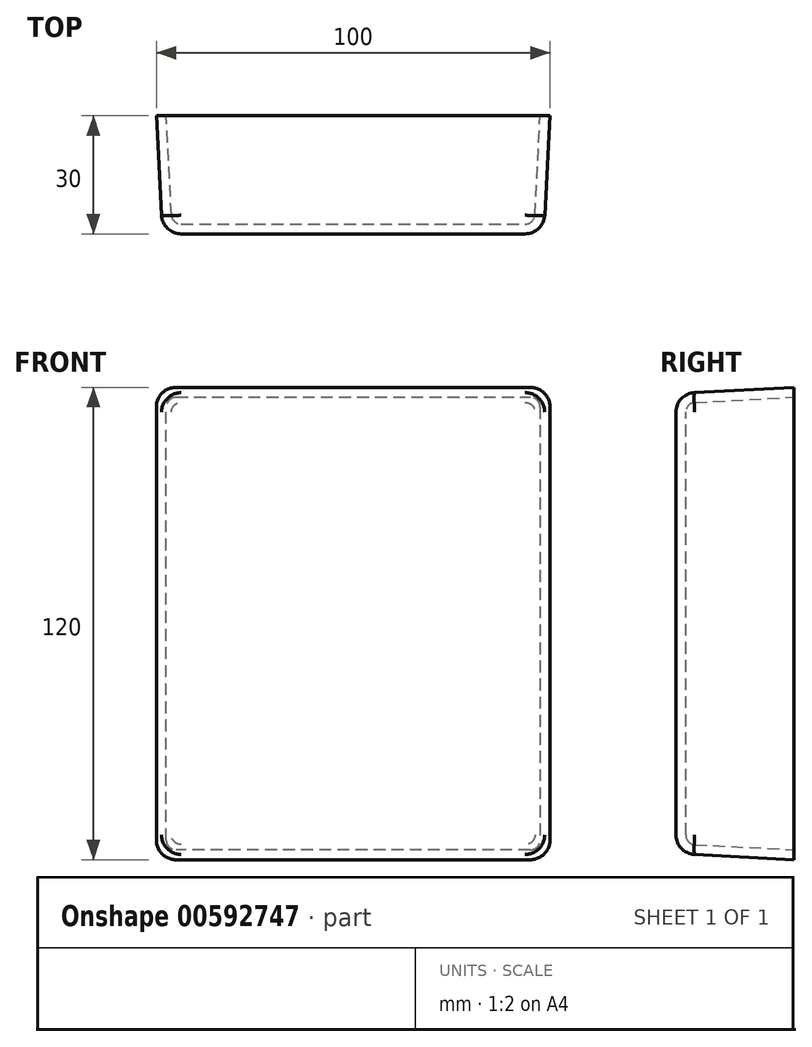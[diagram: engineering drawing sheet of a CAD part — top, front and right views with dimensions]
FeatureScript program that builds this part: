
annotation { "Feature Type Name" : "Feature", "Feature Type Description" : "" }
export const myFeature = defineFeature(function(context is Context, id is Id, definition is map)
    precondition{}
    {
        {
            var Q0;
            Q0=qCreatedBy(makeId("Front.planeOp"),FACE);
            var sketch = newSketch(context, id + "F0", { "sketchPlane" : qUnion([Q0])});
            skLineSegment(sketch, "E0.bottom", {"start": v(50, 60) * mm, "end": v(-50, 60) * mm});
            skLineSegment(sketch, "E0.top", {"start": v(50, -60) * mm, "end": v(-50, -60) * mm});
            skLineSegment(sketch, "E0.left", {"start": v(50, 60) * mm, "end": v(50, -60) * mm});
            skLineSegment(sketch, "E0.right", {"start": v(-50, 60) * mm, "end": v(-50, -60) * mm});
            skPoint(sketch, "E0.middle", {"position": v(0, 0) * mm});
            skSolve(sketch);
        }
        {
            var Q0;
            Q0=makeQuery(id+"F0.imprint","IMPRINT",FACE,{"disambiguationData":[TD([[makeQuery(id+"F0.imprint","IMPRINT",EDGE,{"derivedFrom":sQuery(id+"F0.wireOp",EDGE,"E0.bottom")}),1.0]])]});
            extrude(context, id + "F1", {"entities" : qUnion([Q0]), "depth" : 30 * mm, "offsetDistance" : 25 * mm, "hasDraft" : true, "draftAngle" : 3 * degree, "draftPullDirection" : true});
        }
        {
            var Q0;
            Q0=makeQuery(id+"F1.opExtrude","CAP_FACE",FACE,{"disambiguationData":[OSD([sQuery(id+"F0.wireOp",EDGE,"E0.bottom"),sQuery(id+"F0.wireOp",EDGE,"E0.top"),sQuery(id+"F0.wireOp",EDGE,"E0.left"),sQuery(id+"F0.wireOp",EDGE,"E0.right")])],"isStart":false});
            fillet(context, id + "F2", {"entities" : qUnion([Q0]), "radius" : 5 * mm, "tangentPropagation" : true, "allowEdgeOverflow" : false});
        }
        {
            var Q0;
            Q0=makeQuery(id+"F1.opExtrude","SWEPT_EDGE",EDGE,{"disambiguationData":[OSD([sQuery(id+"F0.wireOp",EDGE,"E0.bottom"),sQuery(id+"F0.wireOp",EDGE,"E0.left")])]});
            var Q1;
            Q1=makeQuery(id+"F1.opExtrude","SWEPT_EDGE",EDGE,{"disambiguationData":[OSD([sQuery(id+"F0.wireOp",EDGE,"E0.top"),sQuery(id+"F0.wireOp",EDGE,"E0.left")])]});
            var Q2;
            Q2=makeQuery(id+"F1.opExtrude","SWEPT_EDGE",EDGE,{"disambiguationData":[OSD([sQuery(id+"F0.wireOp",EDGE,"E0.bottom"),sQuery(id+"F0.wireOp",EDGE,"E0.right")])]});
            var Q3;
            Q3=makeQuery(id+"F1.opExtrude","SWEPT_EDGE",EDGE,{"disambiguationData":[OSD([sQuery(id+"F0.wireOp",EDGE,"E0.top"),sQuery(id+"F0.wireOp",EDGE,"E0.right")])]});
            fillet(context, id + "F3", {"entities" : qUnion([Q0, Q1, Q2, Q3]), "radius" : 5 * mm, "tangentPropagation" : true, "allowEdgeOverflow" : false});
        }
        {
            var Q0;
            Q0=makeQuery(id+"F1.opExtrude","CAP_FACE",FACE,{"disambiguationData":[OSD([sQuery(id+"F0.wireOp",EDGE,"E0.bottom"),sQuery(id+"F0.wireOp",EDGE,"E0.top"),sQuery(id+"F0.wireOp",EDGE,"E0.left"),sQuery(id+"F0.wireOp",EDGE,"E0.right")])],"isStart":true});
            shell(context, id + "F4", {"entities" : qUnion([Q0]), "thickness" : 2.5 * mm});
        }
        {
            var Q0;
            Q0=qCreatedBy(makeId("Top.planeOp"),FACE);
            cPlane(context, id + "F5", {"entities" : qUnion([Q0]), "cplaneType" : CPlaneType.OFFSET, "offset" : 25 * mm, "width" : 150 * mm, "height" : 150 * mm});
        }
    });
